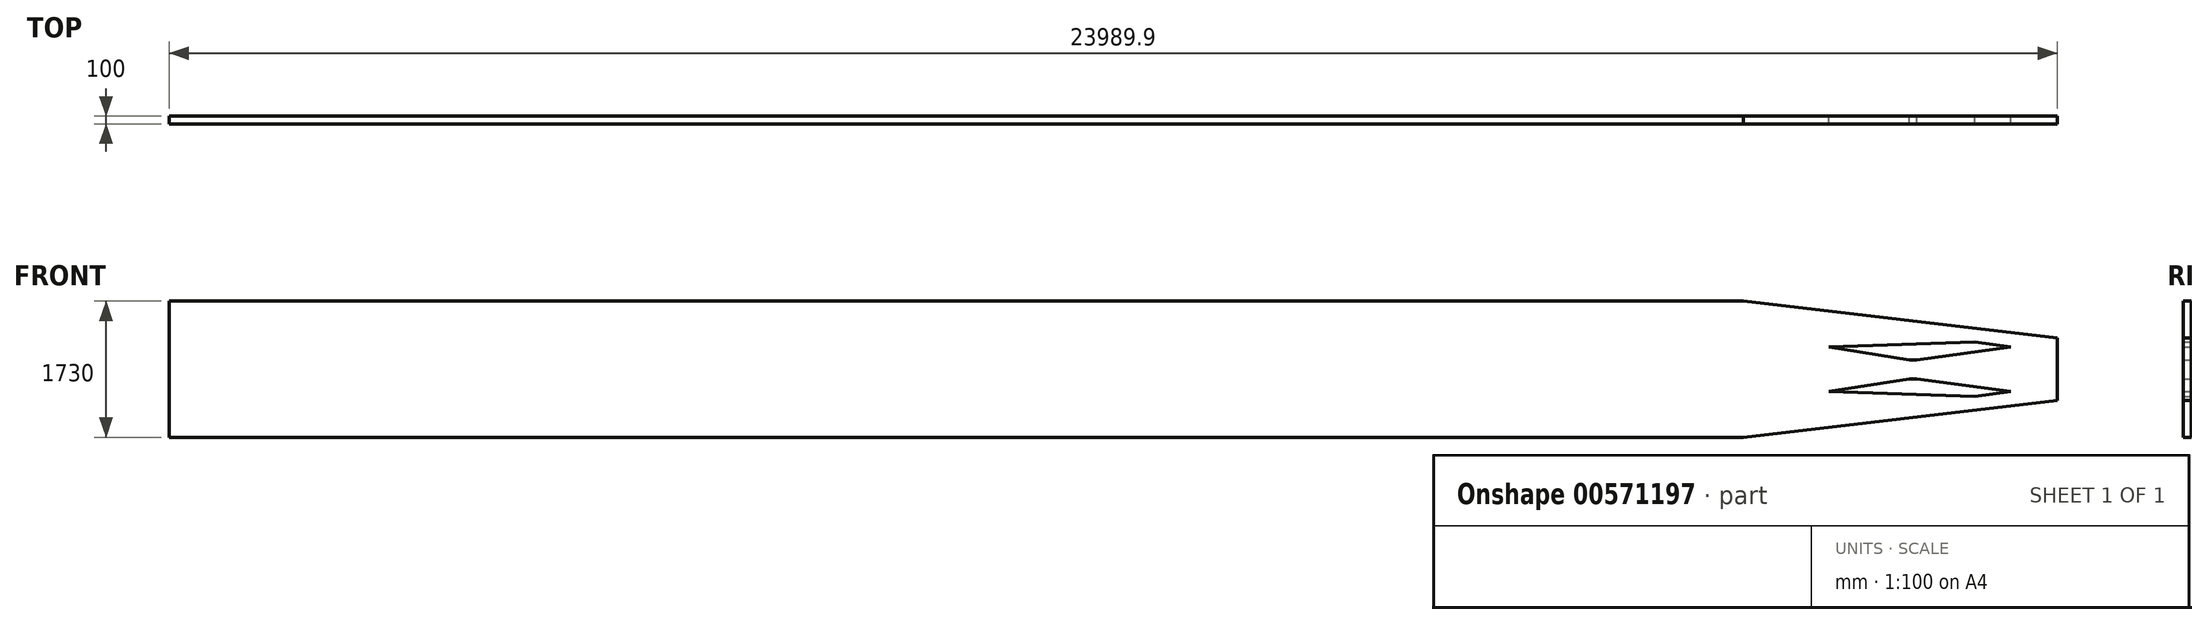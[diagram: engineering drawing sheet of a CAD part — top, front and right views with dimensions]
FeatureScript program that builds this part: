
annotation { "Feature Type Name" : "Feature", "Feature Type Description" : "" }
export const myFeature = defineFeature(function(context is Context, id is Id, definition is map)
    precondition{}
    {
        {
            var Q0;
            Q0=qCreatedBy(makeId("Front.planeOp"),FACE);
            var sketch = newSketch(context, id + "F0", { "sketchPlane" : qUnion([Q0])});
            skPoint(sketch, "E0", {"position": v(0, 865) * mm});
            skPoint(sketch, "E1", {"position": v(3989.9, 398.6) * mm});
            skPoint(sketch, "E2", {"position": v(1088, 281.1) * mm});
            skPoint(sketch, "E3", {"position": v(2941, 346) * mm});
            skPoint(sketch, "E4", {"position": v(3394, 281.1) * mm});
            skPoint(sketch, "E5", {"position": v(2199.8, 121.1) * mm});
            skPoint(sketch, "E6", {"position": v(2107.1, 121.1) * mm});
            skLineSegment(sketch, "E7", {"start": v(1088, 281.1) * mm, "end": v(2107.1, 121.1) * mm});
            skLineSegment(sketch, "E8", {"start": v(2107.1, 121.1) * mm, "end": v(2199.8, 121.1) * mm});
            skLineSegment(sketch, "E9", {"start": v(2199.8, 121.1) * mm, "end": v(3394, 281.1) * mm});
            skLineSegment(sketch, "E10", {"start": v(3394, 281.1) * mm, "end": v(2941, 346) * mm});
            skLineSegment(sketch, "E11", {"start": v(2941, 346) * mm, "end": v(1088, 281.1) * mm});
            skLineSegment(sketch, "E12", {"start": v(3989.9, 398.6) * mm, "end": v(0, 865) * mm});
            skLineSegment(sketch, "E13", {"start": v(0, 865) * mm, "end": v(0, 0) * mm});
            skLineSegment(sketch, "E14", {"start": v(3989.9, 398.6) * mm, "end": v(3989.9, 0) * mm});
            skLineSegment(sketch, "E15", {"start": v(0, 0) * mm, "end": v(3989.9, 0) * mm, "construction": true});
            skLineSegment(sketch, "E16.MirrorCS", {"start": v(0, -865) * mm, "end": v(0, 0) * mm});
            skLineSegment(sketch, "E17.MirrorCS", {"start": v(3989.9, -398.6) * mm, "end": v(0, -865) * mm});
            skLineSegment(sketch, "E18.MirrorCS", {"start": v(2941, -346) * mm, "end": v(1088, -281.1) * mm});
            skLineSegment(sketch, "E19.MirrorCS", {"start": v(3394, -281.1) * mm, "end": v(2941, -346) * mm});
            skLineSegment(sketch, "E20.MirrorCS", {"start": v(2199.8, -121.1) * mm, "end": v(3394, -281.1) * mm});
            skLineSegment(sketch, "E21.MirrorCS", {"start": v(2107.1, -121.1) * mm, "end": v(2199.8, -121.1) * mm});
            skLineSegment(sketch, "E22.MirrorCS", {"start": v(1088, -281.1) * mm, "end": v(2107.1, -121.1) * mm});
            skLineSegment(sketch, "E23.MirrorCS", {"start": v(3989.9, -398.6) * mm, "end": v(3989.9, 0) * mm});
            skSolve(sketch);
        }
        {
            var Q0;
            Q0=makeQuery(id+"F0.imprint","IMPRINT",FACE,{"disambiguationData":[TD([[makeQuery(id+"F0.imprint","IMPRINT",EDGE,{"derivedFrom":sQuery(id+"F0.wireOp",EDGE,"E7")}),-1.0]])]});
            extrude(context, id + "F1", {"entities" : qUnion([Q0]), "depth" : 100 * mm, "offsetDistance" : 25 * mm});
        }
        {
            var Q0;
            Q0=makeQuery(id+"F1.opExtrude","SWEPT_FACE",FACE,{"disambiguationData":[OSD([sQuery(id+"F0.wireOp",EDGE,"E13"),sQuery(id+"F0.wireOp",EDGE,"E16.MirrorCS")])]});
            extrude(context, id + "F2", {"entities" : qUnion([Q0]), "operationType" : NewBodyOperationType.ADD, "depth" : 20000 * mm, "offsetDistance" : 25 * mm});
        }
    });
